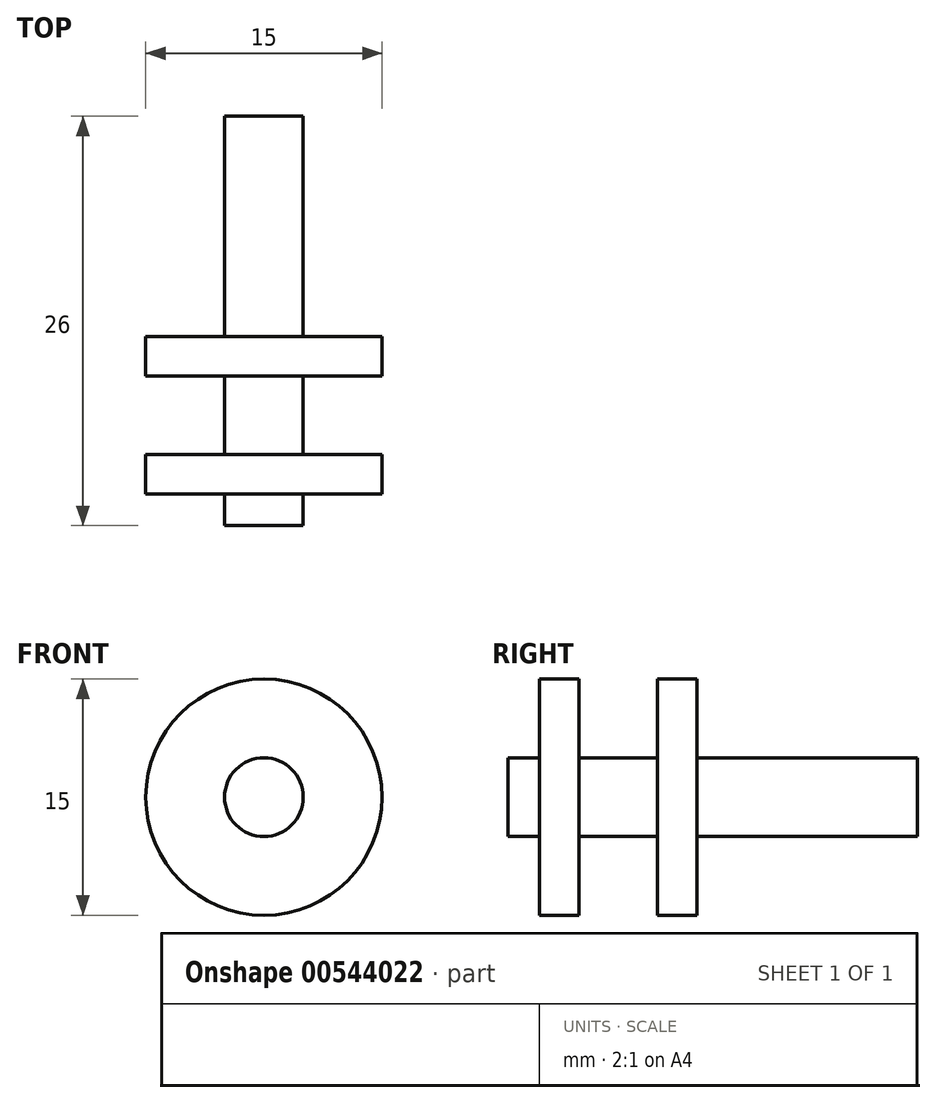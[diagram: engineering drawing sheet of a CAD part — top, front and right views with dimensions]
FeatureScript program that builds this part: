
annotation { "Feature Type Name" : "Feature", "Feature Type Description" : "" }
export const myFeature = defineFeature(function(context is Context, id is Id, definition is map)
    precondition{}
    {
        {
            var Q0;
            Q0=qCreatedBy(makeId("Top.planeOp"),FACE);
            var sketch = newSketch(context, id + "F0", { "sketchPlane" : qUnion([Q0])});
            skLineSegment(sketch, "E0", {"start": v(0, 0) * mm, "end": v(2.5, 0) * mm});
            skLineSegment(sketch, "E1", {"start": v(2.5, 0) * mm, "end": v(2.5, 2) * mm});
            skLineSegment(sketch, "E2", {"start": v(2.5, 2) * mm, "end": v(7.5, 2) * mm});
            skLineSegment(sketch, "E3", {"start": v(7.5, 2) * mm, "end": v(7.5, 4.5) * mm});
            skLineSegment(sketch, "E4", {"start": v(7.5, 4.5) * mm, "end": v(2.5, 4.5) * mm});
            skLineSegment(sketch, "E5", {"start": v(2.5, 4.5) * mm, "end": v(2.5, 9.5) * mm});
            skLineSegment(sketch, "E6", {"start": v(2.5, 9.5) * mm, "end": v(7.5, 9.5) * mm});
            skLineSegment(sketch, "E7", {"start": v(7.5, 9.5) * mm, "end": v(7.5, 12) * mm});
            skLineSegment(sketch, "E8", {"start": v(7.5, 12) * mm, "end": v(2.5, 12) * mm});
            skLineSegment(sketch, "E9", {"start": v(2.5, 12) * mm, "end": v(2.5, 26) * mm});
            skLineSegment(sketch, "E10", {"start": v(2.5, 26) * mm, "end": v(0, 26) * mm});
            skLineSegment(sketch, "E11", {"start": v(0, 26) * mm, "end": v(0, 0) * mm});
            skSolve(sketch);
        }
        {
            var Q0;
            Q0 = qSketchRegion(id + "F0", true);
            var Q1;
            Q1=sQuery(id+"F0.wireOp",EDGE,"E11");
            revolve(context, id + "F1", {"entities" : qUnion([Q0]), "axis" : qUnion([Q1]), "revolveType" : RevolveType.FULL});
        }
    });
